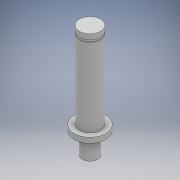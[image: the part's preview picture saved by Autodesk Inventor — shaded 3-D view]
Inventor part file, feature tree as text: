
AUTODESK INVENTOR PART (.ipt)
format: ipt  version: 2018 (Build 220112000, 112)  size: 128,512 bytes
history: native  units: mm
features: revolve x1, sketch x1
ambient origin geometry x8: Origin, YZ Plane, XZ Plane, XY Plane, X Axis, Y Axis, Z Axis, Center Point
bodies: Solid1 (feature_tree)
feature tree (2):
  revolve  "Revolution1"  [1 undecoded]
  sketch  "Sketch1"  dims[d0=4.0mm d1=2.0mm d2=0.2mm d3=0.8mm d4=29.8mm d5=2.0mm d6=2.0mm d8=90.0deg d9=1.0mm d10=8.0mm]
note: 1 required parameter value undecoded (feature->parameter linkage not recoverable at this tier; creation-order binding heuristic only, values carry confidence <= 0.55)
